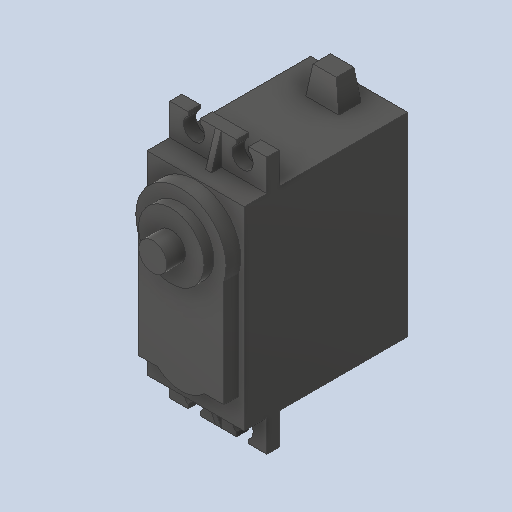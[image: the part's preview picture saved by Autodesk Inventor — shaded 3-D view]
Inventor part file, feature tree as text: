
AUTODESK INVENTOR PART (.ipt)
format: ipt  version: 2022 (Build 260153000, 153)  size: 260,608 bytes
history: native  units: mm
features: sketch x11, extrude x10, chamfer x4, hole x1, mirror x1, projected_geometry x1
ambient origin geometry x8: Origin, YZ Plane, XZ Plane, XY Plane, X Axis, Y Axis, Z Axis, Center Point
bodies: Solid1 (feature_tree)
feature tree (28):
  extrude  "Extrusion1"  Depth=40.0mm
  extrude  "Extrusion2"  Depth=53.0mm
  hole  "Hole1"  [1 undecoded]
  extrude  "Extrusion3"  Depth=2.5mm
  extrude  "Extrusion4"  Depth=2.5mm
  mirror  "Mirror1"
  extrude  "Extrusion5"  Depth=2.5mm TaperAngle=0.0deg
  extrude  "Extrusion6"  Depth=1.2mm TaperAngle=0.0deg
  extrude  "Extrusion7"  Depth=13.5mm
  extrude  "Extrusion8"  Depth=5.0mm
  extrude  "Extrusion9"  Depth=17.7mm
  chamfer  "Chamfer1"  Distance=34.4mm
  chamfer  "Chamfer2"  Distance=3.0mm
  chamfer  "Chamfer3"  Distance=9.6mm
  chamfer  "Chamfer4"  Distance=36.35mm
  extrude  "Extrusion10"  Depth=3.0mm TaperAngle=0.0deg
  sketch  "Sketch1"  dims[d0=20.0mm d1=40.0mm]
  sketch  "Sketch2"  dims[d2=7.2mm d3=26.5mm d4=0.0mm d5=0.0mm d6=53.0mm]
  sketch  "Sketch3"  dims[d7=2.5mm d8=0.0mm d9=47.85mm]
  sketch  "Sketch4"  dims[d10=10.0mm]
  sketch  "Sketch5"  dims[d11=4.35mm d12=6.0mm d13=4.0mm d14=2.0mm d15=90.0deg d16=8.0mm d17=20.594885mm d18=2.5mm]
  sketch  "Sketch6"  dims[d19=2.5mm d20=2.5mm]
  sketch  "Sketch7"  dims[d21=2.5mm d22=2.5mm d23=0.0mm]
  sketch  "Sketch8"  dims[d24=2.0mm d25=1.2mm d26=0.0mm]
  sketch  "Sketch9"  dims[d27=30.5mm d28=13.5mm]
  sketch  "Sketch10"  dims[d29=5.0mm d30=0.0mm d31=18.6mm]
  projected_geometry  "Projected Loop1"
  sketch  "Sketch11"  dims[d32=3.0mm d33=0.0mm d34=17.7mm d35=34.4mm d36=3.0mm d37=0.0mm d38=9.6mm d39=36.35mm d40=3.0mm d41=0.0mm d42=3.0mm d43=4.6mm d44=6.8mm d45=6.0mm d46=0.0mm d47=6.0mm d48=1.0mm d49=45.0deg d50=6.0mm d51=1.0mm d52=45.0deg d53=6.0mm d54=0.5mm d55=45.0deg d56=6.0mm d57=0.5mm d58=45.0deg d59=5.8mm d60=3.8mm d61=0.0mm]
note: 1 required parameter value undecoded (feature->parameter linkage not recoverable at this tier; creation-order binding heuristic only, values carry confidence <= 0.55)
